# Revit family: 0053303 Feilo Sylvania Lighting Fixture SYLFLAT SURFACE 1400 R 4000K
name_source: partatom
category: Lighting Fixtures
revit_build: Autodesk Revit 2016 (Build: 20150220_1215(x64)
units: mm (PartAtom-declared; Revit-internal decimal feet)

## family parameters
Cut with Voids When Loaded = No
Host = Face
Light Source = Yes
OmniClass Number = 23.80.70.00
OmniClass Title = Lighting
Part Type = Normal
Room Calculation Point = No
Round Connector Dimension = Use Diameter
Shared = No

## types (1)
- 0053303 SYLFLAT SURFACE 1400 R 4000K
    Apparent Load = 18 VA
    Assembly Code = D5020200
    AssetType = Fixed
    Circle_FEILO = Yes
    ClassificationName = Uniclass2015
    ClassificationValue = EF_70_80
    Color Filter = 16777215
    Cost = 0 $
    Default Elevation = 1219 mm
    Description = Integrated round surface mounted 220mm diameter LED downlight providing uniform distribution with an opal diffuser, 110° beam angle, 1500LM, 18W, 83lm/W, 4000K, CRI80, non-dimmable, IP20, IK06, 25,000hrs (L70)
    Diameter_FEILO = 220 mm  [stored 0.721785 ft]
    Dimming Lamp Color Temperature Shift = <None>
    DimmingControlOptions = Non dimmable
    DocumentationLiterature = http://www.feilosylvania.com
    DurationUnit = hours
    ElectricShockClassification = Class II
    Emit Shape Visible in Rendering = No
    Emit from Circle Diameter = 180 mm  [stored 0.590551 ft]
    ExpectedLife = 50000
    Height_FEILO = 40 mm  [stored 0.131234 ft]
    IfcExportAs = IfcLightFixtureType
    IfcExportType = IfcLightFixtureType
    ImpactProtectionIndex = IK06
    IngressProtection = IP20
    InputVoltage = 220-240V~
    Keynote = 16500
    Lamp = LED
    LampColourRenderingIndex = 0
    LampColourTemperature = 4000 K
    LampNominalLuminous = 1500 lm
    LampsType = LED
    LightOutputRatio = 100
    LuminousEfficacy = 83 lm/W
    Manufacturer = Feilo Sylvania
    ManufacturerName = Feilo Sylvania
    Material = plastic housing, polycarbonate diffuser
    Material_1_FEILO = Body-Sylvania-SylFlat-White
    Material_2_FEILO = Diffuser-Sylvania-SylFlat-Opaque
    Material_3_FEILO = <By Category>
    Material_4_FEILO = <By Category>
    Model = SYLFLAT SURFACE 1400 R 4000K
    ModelNumber = 0053303
    ModelReference = SYLFLAT SURFACE 1400 R 4000K
    Name = SYLFLAT SURFACE 1400 R 4000K
    NominalDepth = 0 mm  [stored 0 ft]
    NominalHeight = 40 mm  [stored 0.131234 ft]
    NominalLength = 0 mm  [stored 0 ft]
    Photometric Web File = 0053303.ies
    PowerConsumption = 18 W
    PowerFactor = 0.9
    Square_FEILO = No
    Tilt Angle = -90.00°
    Type Image = <None>
    TypeName = SYLFLAT SURFACE 1400 R 4000K
    URL = http://www.feilosylvania.com
    Voltage = 230 V
    Weight = 5.58 kg

note: [stored X ft] marks values corroborated as IEEE doubles in the binary element streams (Revit-internal decimal feet)

## geometry (parser evidence)
native form markers: Sweep x3
no freeform markers — native parametric forms only
